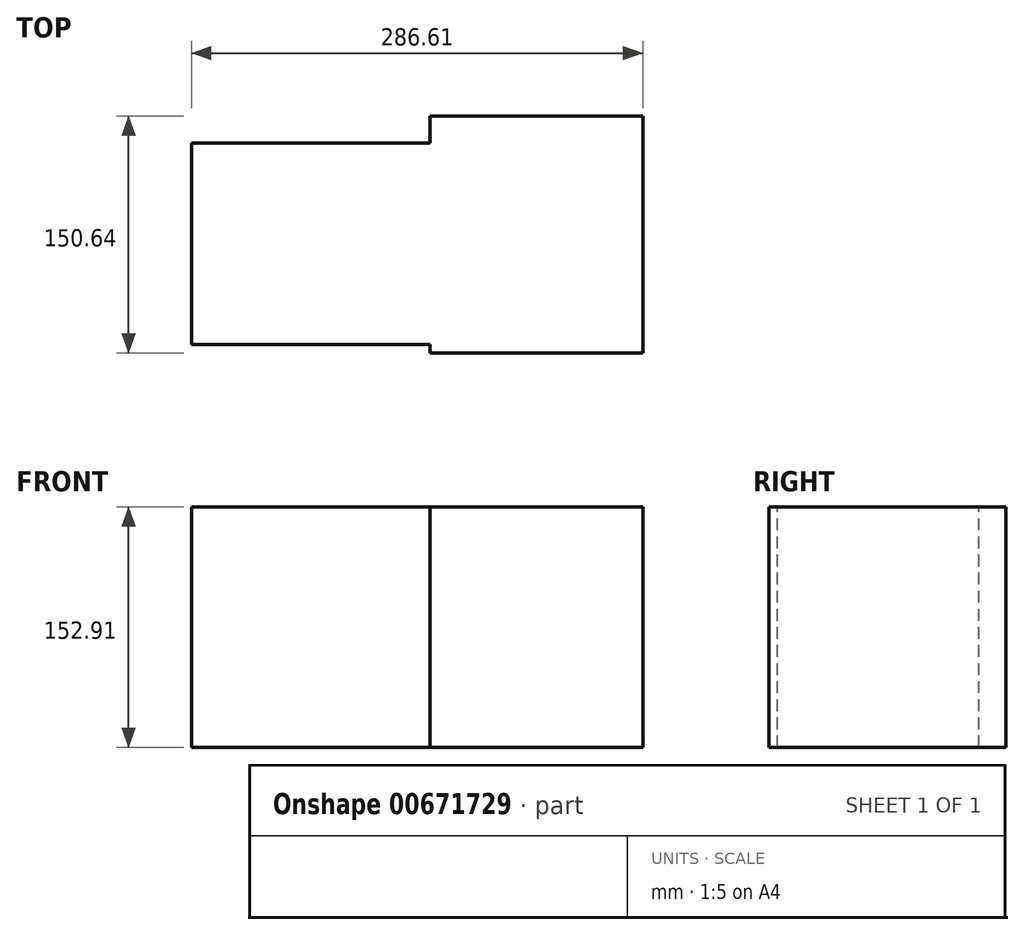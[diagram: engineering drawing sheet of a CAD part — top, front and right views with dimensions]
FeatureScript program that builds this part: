
annotation { "Feature Type Name" : "Feature", "Feature Type Description" : "" }
export const myFeature = defineFeature(function(context is Context, id is Id, definition is map)
    precondition{}
    {
        {
            var Q0;
            Q0=qCreatedBy(makeId("Top.planeOp"),FACE);
            var sketch = newSketch(context, id + "F0", { "sketchPlane" : qUnion([Q0])});
            skLineSegment(sketch, "E0.bottom", {"start": v(-201.17, 32.58) * mm, "end": v(-49.64, 32.58) * mm});
            skLineSegment(sketch, "E0.top", {"start": v(-201.17, -95.5) * mm, "end": v(-49.64, -95.5) * mm});
            skLineSegment(sketch, "E0.left", {"start": v(-201.17, 32.58) * mm, "end": v(-201.17, -95.5) * mm});
            skLineSegment(sketch, "E1.bottom", {"start": v(-49.64, 49.68) * mm, "end": v(85.44, 49.68) * mm});
            skLineSegment(sketch, "E1.top", {"start": v(-49.64, -100.96) * mm, "end": v(85.44, -100.96) * mm});
            skLineSegment(sketch, "E1.left", {"start": v(-49.64, 49.68) * mm, "end": v(-49.64, 32.58) * mm});
            skLineSegment(sketch, "E1.right", {"start": v(85.44, 49.68) * mm, "end": v(85.44, -100.96) * mm});
            skLineSegment(sketch, "E2.trimOffspring", {"start": v(-49.64, -95.5) * mm, "end": v(-49.64, -100.96) * mm});
            skLineSegment(sketch, "E3.1.0.0", {"start": v(-65.44, 79.54) * mm, "end": v(-65.44, 62.44) * mm});
            skLineSegment(sketch, "E3.1.0.1", {"start": v(-216.97, 62.44) * mm, "end": v(-65.44, 62.44) * mm});
            skLineSegment(sketch, "E3.1.0.2", {"start": v(-216.97, -65.65) * mm, "end": v(-65.44, -65.65) * mm});
            skLineSegment(sketch, "E3.1.0.3", {"start": v(-216.97, 62.44) * mm, "end": v(-216.97, -65.65) * mm});
            skLineSegment(sketch, "E3.2.0.0", {"start": v(-81.24, 109.4) * mm, "end": v(-81.24, 92.3) * mm});
            skLineSegment(sketch, "E3.2.0.1", {"start": v(-232.78, 92.3) * mm, "end": v(-81.24, 92.3) * mm});
            skLineSegment(sketch, "E3.2.0.2", {"start": v(-232.78, -35.79) * mm, "end": v(-81.24, -35.79) * mm});
            skLineSegment(sketch, "E3.2.0.3", {"start": v(-232.78, 92.3) * mm, "end": v(-232.78, -35.79) * mm});
            skLineSegment(sketch, "E3.direction1", {"start": v(-201.17, -95.5) * mm, "end": v(-216.97, -65.65) * mm, "construction": true});
            skSolve(sketch);
        }
        {
            var Q0;
            {var subQ3=sQuery(id+"F0.wireOp",EDGE,"E0.bottom");Q0=makeQuery(id+"F0.imprint","IMPRINT",FACE,{"disambiguationData":[TD([[makeQuery(id+"F0.imprint","IMPRINT",EDGE,{"derivedFrom":subQ3}),-1.0]])]});}
            extrude(context, id + "F1", {"entities" : qUnion([Q0]), "oppositeDirection" : true, "depth" : 152.9 * mm, "offsetDistance" : 25.4 * mm});
        }
    });
